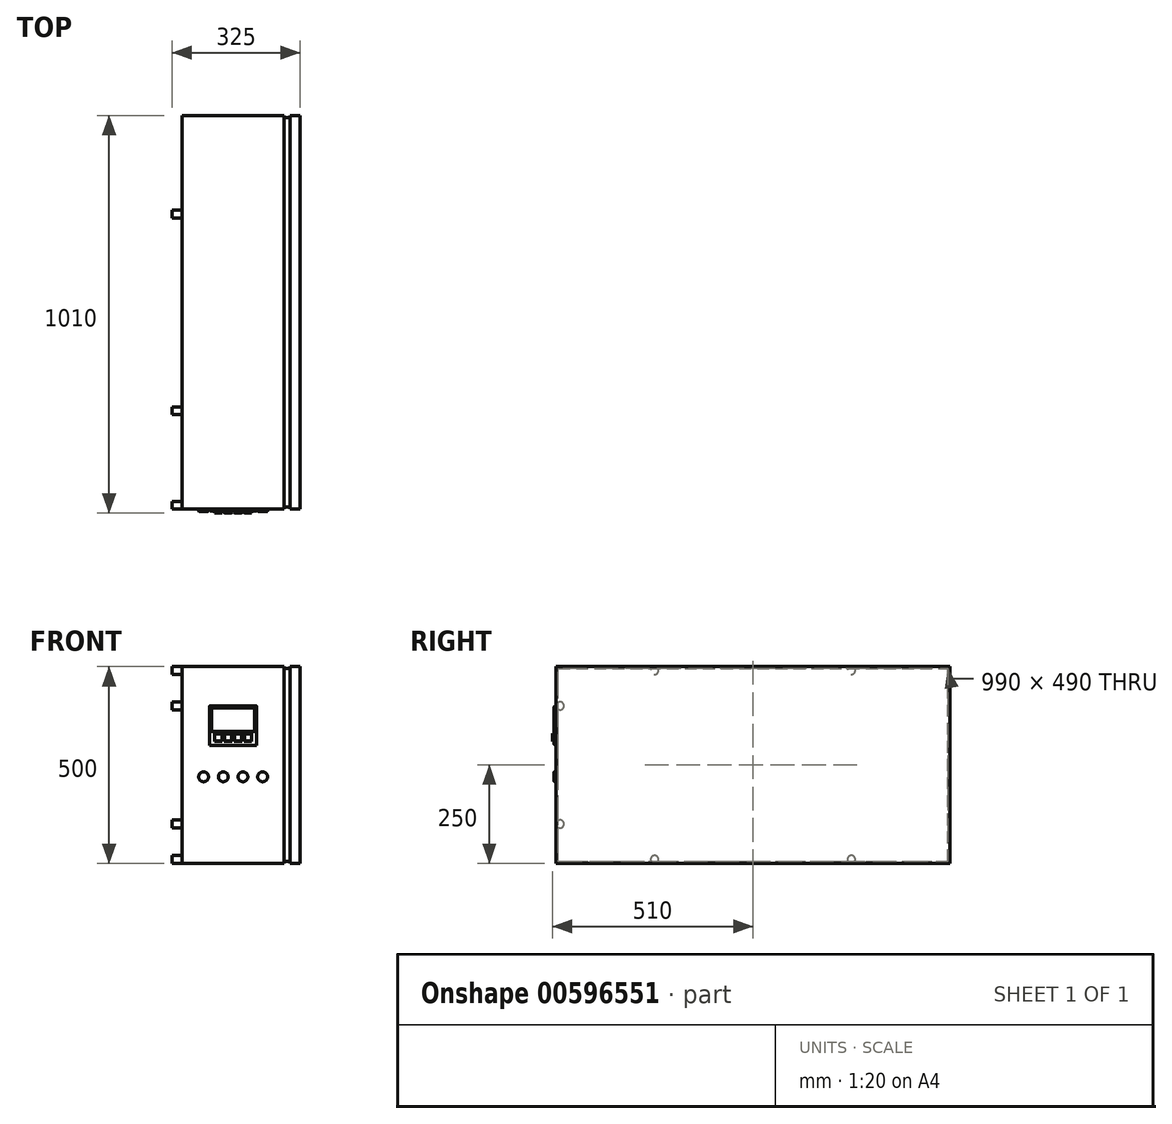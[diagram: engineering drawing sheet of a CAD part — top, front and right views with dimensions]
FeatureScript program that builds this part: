
annotation { "Feature Type Name" : "Feature", "Feature Type Description" : "" }
export const myFeature = defineFeature(function(context is Context, id is Id, definition is map)
    precondition{}
    {
        {
            var Q0;
            Q0=qCreatedBy(makeId("Front.planeOp"),FACE);
            var sketch = newSketch(context, id + "F0", { "sketchPlane" : qUnion([Q0])});
            skPoint(sketch, "E0.0", {"position": v(0, 0) * mm});
            skLineSegment(sketch, "E1.bottom", {"start": v(0, 0) * mm, "end": v(300, 0) * mm});
            skLineSegment(sketch, "E1.top", {"start": v(0, 500) * mm, "end": v(300, 500) * mm});
            skLineSegment(sketch, "E1.left", {"start": v(0, 0) * mm, "end": v(0, 500) * mm});
            skLineSegment(sketch, "E1.right", {"start": v(300, 0) * mm, "end": v(300, 500) * mm});
            skSolve(sketch);
        }
        {
            var Q0;
            Q0 = qSketchRegion(id + "F0", true);
            extrude(context, id + "F1", {"entities" : qUnion([Q0]), "depth" : 1000 * mm, "offsetDistance" : 25 * mm});
        }
        {
            var Q0;
            Q0=makeQuery(id+"F1.opExtrude","SWEPT_FACE",FACE,{"disambiguationData":[OSD([sQuery(id+"F0.wireOp",EDGE,"E1.right")])]});
            cPlane(context, id + "F2", {"entities" : qUnion([Q0]), "cplaneType" : CPlaneType.OFFSET, "offset" : 25 * mm, "oppositeDirection" : true, "width" : 150 * mm, "height" : 150 * mm});
        }
        {
            var Q0;
            Q0=qCreatedBy(id+"F2.planeOp",FACE);
            var sketch = newSketch(context, id + "F3", { "sketchPlane" : qUnion([Q0])});
            skLineSegment(sketch, "E2.bottom", {"start": v(-1000, 0) * mm, "end": v(0, 0) * mm});
            skLineSegment(sketch, "E2.top", {"start": v(-1000, 500) * mm, "end": v(0, 500) * mm});
            skLineSegment(sketch, "E2.left", {"start": v(-1000, 0) * mm, "end": v(-1000, 500) * mm});
            skLineSegment(sketch, "E2.right", {"start": v(0, 0) * mm, "end": v(0, 500) * mm});
            skLineSegment(sketch, "E3.bottom", {"start": v(-995, 5) * mm, "end": v(-5, 5) * mm});
            skLineSegment(sketch, "E3.top", {"start": v(-995, 495) * mm, "end": v(-5, 495) * mm});
            skLineSegment(sketch, "E3.left", {"start": v(-995, 5) * mm, "end": v(-995, 495) * mm});
            skLineSegment(sketch, "E3.right", {"start": v(-5, 5) * mm, "end": v(-5, 495) * mm});
            skSolve(sketch);
        }
        {
            var Q0;
            Q0 = qSketchRegion(id + "F3", true);
            extrude(context, id + "F4", {"entities" : qUnion([Q0]), "operationType" : NewBodyOperationType.REMOVE, "oppositeDirection" : true, "depth" : 15 * mm, "offsetDistance" : 25 * mm});
        }
        {
            var Q0;
            Q0=makeQuery(id+"F1.opExtrude","SWEPT_FACE",FACE,{"disambiguationData":[OSD([sQuery(id+"F0.wireOp",EDGE,"E1.left")])]});
            var sketch = newSketch(context, id + "F5", { "sketchPlane" : qUnion([Q0])});
            skCircle(sketch, "E4", {"center": v(250, 490) * mm, "radius": 10 * mm});
            skCircle(sketch, "E5", {"center": v(750, 490) * mm, "radius": 10 * mm});
            skCircle(sketch, "E6", {"center": v(250, 10) * mm, "radius": 10 * mm});
            skCircle(sketch, "E7", {"center": v(750, 10) * mm, "radius": 10 * mm});
            skCircle(sketch, "E8", {"center": v(990, 100) * mm, "radius": 10 * mm});
            skCircle(sketch, "E9", {"center": v(990, 400) * mm, "radius": 10 * mm});
            skSolve(sketch);
        }
        {
            var Q0;
            Q0 = qSketchRegion(id + "F5", true);
            extrude(context, id + "F6", {"entities" : qUnion([Q0]), "operationType" : NewBodyOperationType.ADD, "depth" : 25 * mm, "offsetDistance" : 25 * mm});
        }
        {
            var Q0;
            {var subQ0=sQuery(id+"F0.wireOp",EDGE,"E1.bottom");var subQ1=sQuery(id+"F0.wireOp",EDGE,"E1.top");var subQ2=sQuery(id+"F0.wireOp",EDGE,"E1.left");Q0=makeQuery(id+"F4.boolean.opBoolean","SPLIT",FACE,{"disambiguationData":[TD([makeQuery(id+"F1.opExtrude","SWEPT_FACE",FACE,{"disambiguationData":[OSD([subQ2])]})])],"derivedFrom":makeQuery(id+"F1.opExtrude","CAP_FACE",FACE,{"disambiguationData":[OSD([subQ0,subQ1,subQ2,sQuery(id+"F0.wireOp",EDGE,"E1.right")])],"isStart":false})});}
            var sketch = newSketch(context, id + "F7", { "sketchPlane" : qUnion([Q0])});
            skLineSegment(sketch, "E10.bottom", {"start": v(70, 400) * mm, "end": v(190, 400) * mm});
            skLineSegment(sketch, "E10.top", {"start": v(70, 300) * mm, "end": v(190, 300) * mm});
            skLineSegment(sketch, "E10.left", {"start": v(70, 400) * mm, "end": v(70, 300) * mm});
            skLineSegment(sketch, "E10.right", {"start": v(190, 400) * mm, "end": v(190, 300) * mm});
            skSolve(sketch);
        }
        {
            var Q0;
            Q0=makeQuery(id+"F7.imprint","IMPRINT",FACE,{"disambiguationData":[TD([[makeQuery(id+"F7.imprint","IMPRINT",EDGE,{"derivedFrom":sQuery(id+"F7.wireOp",EDGE,"E10.bottom")}),-1.0]])]});
            extrude(context, id + "F8", {"entities" : qUnion([Q0]), "depth" : 5 * mm, "offsetDistance" : 25 * mm});
        }
        {
            var Q0;
            Q0=makeQuery(id+"F8.opExtrude","CAP_FACE",FACE,{"disambiguationData":[OSD([sQuery(id+"F7.wireOp",EDGE,"E10.bottom"),sQuery(id+"F7.wireOp",EDGE,"E10.top"),sQuery(id+"F7.wireOp",EDGE,"E10.left"),sQuery(id+"F7.wireOp",EDGE,"E10.right")])],"isStart":false});
            var sketch = newSketch(context, id + "F9", { "sketchPlane" : qUnion([Q0])});
            skLineSegment(sketch, "E11.bottom", {"start": v(82.5, 330) * mm, "end": v(102.5, 330) * mm});
            skLineSegment(sketch, "E11.top", {"start": v(82.5, 310) * mm, "end": v(102.5, 310) * mm});
            skLineSegment(sketch, "E11.left", {"start": v(82.5, 330) * mm, "end": v(82.5, 310) * mm});
            skLineSegment(sketch, "E11.right", {"start": v(102.5, 330) * mm, "end": v(102.5, 310) * mm});
            skLineSegment(sketch, "E12.1.0.0", {"start": v(107.5, 330) * mm, "end": v(127.5, 330) * mm});
            skLineSegment(sketch, "E12.1.0.1", {"start": v(127.5, 330) * mm, "end": v(127.5, 310) * mm});
            skLineSegment(sketch, "E12.1.0.2", {"start": v(107.5, 310) * mm, "end": v(127.5, 310) * mm});
            skLineSegment(sketch, "E12.1.0.3", {"start": v(107.5, 330) * mm, "end": v(107.5, 310) * mm});
            skLineSegment(sketch, "E12.2.0.0", {"start": v(132.5, 330) * mm, "end": v(152.5, 330) * mm});
            skLineSegment(sketch, "E12.2.0.1", {"start": v(152.5, 330) * mm, "end": v(152.5, 310) * mm});
            skLineSegment(sketch, "E12.2.0.2", {"start": v(132.5, 310) * mm, "end": v(152.5, 310) * mm});
            skLineSegment(sketch, "E12.2.0.3", {"start": v(132.5, 330) * mm, "end": v(132.5, 310) * mm});
            skLineSegment(sketch, "E12.3.0.0", {"start": v(157.5, 330) * mm, "end": v(177.5, 330) * mm});
            skLineSegment(sketch, "E12.3.0.1", {"start": v(177.5, 330) * mm, "end": v(177.5, 310) * mm});
            skLineSegment(sketch, "E12.3.0.2", {"start": v(157.5, 310) * mm, "end": v(177.5, 310) * mm});
            skLineSegment(sketch, "E12.3.0.3", {"start": v(157.5, 330) * mm, "end": v(157.5, 310) * mm});
            skLineSegment(sketch, "E12.direction1", {"start": v(82.5, 330) * mm, "end": v(107.5, 330) * mm, "construction": true});
            skSolve(sketch);
        }
        {
            var Q0;
            Q0=makeQuery(id+"F9.imprint","IMPRINT",FACE,{"disambiguationData":[TD([[makeQuery(id+"F9.imprint","IMPRINT",EDGE,{"derivedFrom":sQuery(id+"F9.wireOp",EDGE,"E11.bottom")}),-1.0]])]});
            var Q1;
            Q1=makeQuery(id+"F9.imprint","IMPRINT",FACE,{"disambiguationData":[TD([[makeQuery(id+"F9.imprint","IMPRINT",EDGE,{"derivedFrom":sQuery(id+"F9.wireOp",EDGE,"E12.1.0.0")}),-1.0]])]});
            var Q2;
            Q2=makeQuery(id+"F9.imprint","IMPRINT",FACE,{"disambiguationData":[TD([[makeQuery(id+"F9.imprint","IMPRINT",EDGE,{"derivedFrom":sQuery(id+"F9.wireOp",EDGE,"E12.2.0.0")}),-1.0]])]});
            var Q3;
            Q3=makeQuery(id+"F9.imprint","IMPRINT",FACE,{"disambiguationData":[TD([[makeQuery(id+"F9.imprint","IMPRINT",EDGE,{"derivedFrom":sQuery(id+"F9.wireOp",EDGE,"E12.3.0.0")}),-1.0]])]});
            extrude(context, id + "F10", {"entities" : qUnion([Q0, Q1, Q2, Q3]), "operationType" : NewBodyOperationType.ADD, "depth" : 5 * mm, "offsetDistance" : 25 * mm});
        }
        {
            var Q0;
            Q0=makeQuery(id+"F8.opExtrude","CAP_FACE",FACE,{"disambiguationData":[OSD([sQuery(id+"F7.wireOp",EDGE,"E10.bottom"),sQuery(id+"F7.wireOp",EDGE,"E10.top"),sQuery(id+"F7.wireOp",EDGE,"E10.left"),sQuery(id+"F7.wireOp",EDGE,"E10.right")])],"isStart":false});
            var sketch = newSketch(context, id + "F11", { "sketchPlane" : qUnion([Q0])});
            skLineSegment(sketch, "E13.bottom", {"start": v(75, 395) * mm, "end": v(185, 395) * mm});
            skLineSegment(sketch, "E13.top", {"start": v(75, 335) * mm, "end": v(185, 335) * mm});
            skLineSegment(sketch, "E13.left", {"start": v(75, 395) * mm, "end": v(75, 335) * mm});
            skLineSegment(sketch, "E13.right", {"start": v(185, 395) * mm, "end": v(185, 335) * mm});
            skSolve(sketch);
        }
        {
            var Q0;
            Q0=makeQuery(id+"F11.imprint","IMPRINT",FACE,{"disambiguationData":[TD([[makeQuery(id+"F11.imprint","IMPRINT",EDGE,{"derivedFrom":sQuery(id+"F11.wireOp",EDGE,"E13.bottom")}),-1.0]])]});
            extrude(context, id + "F12", {"entities" : qUnion([Q0]), "operationType" : NewBodyOperationType.REMOVE, "oppositeDirection" : true, "depth" : 2 * mm, "offsetDistance" : 25 * mm});
        }
        {
            var Q0;
            {var subQ0=sQuery(id+"F0.wireOp",EDGE,"E1.bottom");var subQ1=sQuery(id+"F0.wireOp",EDGE,"E1.top");var subQ2=sQuery(id+"F0.wireOp",EDGE,"E1.left");Q0=makeQuery(id+"F4.boolean.opBoolean","SPLIT",FACE,{"disambiguationData":[TD([makeQuery(id+"F1.opExtrude","SWEPT_FACE",FACE,{"disambiguationData":[OSD([subQ2])]})])],"derivedFrom":makeQuery(id+"F1.opExtrude","CAP_FACE",FACE,{"disambiguationData":[OSD([subQ0,subQ1,subQ2,sQuery(id+"F0.wireOp",EDGE,"E1.right")])],"isStart":false})});}
            var sketch = newSketch(context, id + "F13", { "sketchPlane" : qUnion([Q0])});
            skSolve(sketch);
        }
        {
            var Q0;
            {var subQ0=sQuery(id+"F0.wireOp",EDGE,"E1.left");Q0=makeQuery(id+"F13.imprint","IMPRINT",FACE,{"disambiguationData":[TD([[makeQuery(id+"F13.imprint","IMPRINT",EDGE,{"derivedFrom":makeQuery(id+"F1.opExtrude","CAP_EDGE",EDGE,{"disambiguationData":[OSD([subQ0])],"isStart":false})}),-1.0]])]});}
            var sketch = newSketch(context, id + "F14", { "sketchPlane" : qUnion([Q0])});
            skCircle(sketch, "E14", {"center": v(55, 220) * mm, "radius": 12.5 * mm});
            skCircle(sketch, "E15.1.0.0", {"center": v(105, 220) * mm, "radius": 12.5 * mm});
            skCircle(sketch, "E15.2.0.0", {"center": v(155, 220) * mm, "radius": 12.5 * mm});
            skCircle(sketch, "E15.3.0.0", {"center": v(205, 220) * mm, "radius": 12.5 * mm});
            skLineSegment(sketch, "E15.direction1", {"start": v(55, 220) * mm, "end": v(105, 220) * mm, "construction": true});
            skSolve(sketch);
        }
        {
            var Q0;
            Q0 = qSketchRegion(id + "F14", true);
            extrude(context, id + "F15", {"entities" : qUnion([Q0]), "depth" : 6 * mm, "offsetDistance" : 25 * mm});
        }
        {
            var Q0;
            Q0=makeQuery(id+"F15.opExtrude","CAP_EDGE",EDGE,{"disambiguationData":[OSD([sQuery(id+"F14.wireOp",EDGE,"E14")])],"isStart":false});
            var Q1;
            Q1=makeQuery(id+"F15.opExtrude","CAP_EDGE",EDGE,{"disambiguationData":[OSD([sQuery(id+"F14.wireOp",EDGE,"E15.1.0.0")])],"isStart":false});
            var Q2;
            Q2=makeQuery(id+"F15.opExtrude","CAP_EDGE",EDGE,{"disambiguationData":[OSD([sQuery(id+"F14.wireOp",EDGE,"E15.2.0.0")])],"isStart":false});
            var Q3;
            Q3=makeQuery(id+"F15.opExtrude","CAP_EDGE",EDGE,{"disambiguationData":[OSD([sQuery(id+"F14.wireOp",EDGE,"E15.3.0.0")])],"isStart":false});
            fillet(context, id + "F16", {"entities" : qUnion([Q0, Q1, Q2, Q3]), "radius" : 2 * mm, "tangentPropagation" : true, "allowEdgeOverflow" : false});
        }
        {
            var Q0;
            Q0=makeQuery(id+"F8.opExtrude","CAP_EDGE",EDGE,{"disambiguationData":[OSD([sQuery(id+"F7.wireOp",EDGE,"E10.left")])],"isStart":false});
            var Q1;
            Q1=makeQuery(id+"F8.opExtrude","CAP_EDGE",EDGE,{"disambiguationData":[OSD([sQuery(id+"F7.wireOp",EDGE,"E10.top")])],"isStart":false});
            var Q2;
            Q2=makeQuery(id+"F8.opExtrude","CAP_EDGE",EDGE,{"disambiguationData":[OSD([sQuery(id+"F7.wireOp",EDGE,"E10.right")])],"isStart":false});
            var Q3;
            Q3=makeQuery(id+"F8.opExtrude","CAP_EDGE",EDGE,{"disambiguationData":[OSD([sQuery(id+"F7.wireOp",EDGE,"E10.bottom")])],"isStart":false});
            fillet(context, id + "F17", {"entities" : qUnion([Q0, Q1, Q2, Q3]), "radius" : 3 * mm, "tangentPropagation" : true, "allowEdgeOverflow" : false});
        }
        {
            var Q0;
            Q0=makeQuery(id+"F10.opExtrude","CAP_FACE",FACE,{"disambiguationData":[OSD([sQuery(id+"F9.wireOp",EDGE,"E11.bottom"),sQuery(id+"F9.wireOp",EDGE,"E11.top"),sQuery(id+"F9.wireOp",EDGE,"E11.left"),sQuery(id+"F9.wireOp",EDGE,"E11.right")])],"isStart":false});
            var Q1;
            Q1=makeQuery(id+"F10.opExtrude","CAP_FACE",FACE,{"disambiguationData":[OSD([sQuery(id+"F9.wireOp",EDGE,"E12.1.0.0"),sQuery(id+"F9.wireOp",EDGE,"E12.1.0.1"),sQuery(id+"F9.wireOp",EDGE,"E12.1.0.2"),sQuery(id+"F9.wireOp",EDGE,"E12.1.0.3")])],"isStart":false});
            var Q2;
            Q2=makeQuery(id+"F10.opExtrude","CAP_FACE",FACE,{"disambiguationData":[OSD([sQuery(id+"F9.wireOp",EDGE,"E12.2.0.0"),sQuery(id+"F9.wireOp",EDGE,"E12.2.0.1"),sQuery(id+"F9.wireOp",EDGE,"E12.2.0.2"),sQuery(id+"F9.wireOp",EDGE,"E12.2.0.3")])],"isStart":false});
            var Q3;
            Q3=makeQuery(id+"F10.opExtrude","CAP_FACE",FACE,{"disambiguationData":[OSD([sQuery(id+"F9.wireOp",EDGE,"E12.3.0.0"),sQuery(id+"F9.wireOp",EDGE,"E12.3.0.1"),sQuery(id+"F9.wireOp",EDGE,"E12.3.0.2"),sQuery(id+"F9.wireOp",EDGE,"E12.3.0.3")])],"isStart":false});
            chamfer(context, id + "F18", {"entities" : qUnion([Q0, Q1, Q2, Q3]), "width" : 1 * mm, "tangentPropagation" : true});
        }
        {
            var Q0;
            Q0=makeQuery(id+"F12.boolean.opBoolean","COPY",FACE,{"derivedFrom":makeQuery(id+"F12.opExtrude","CAP_FACE",FACE,{"disambiguationData":[OSD([sQuery(id+"F11.wireOp",EDGE,"E13.bottom"),sQuery(id+"F11.wireOp",EDGE,"E13.top"),sQuery(id+"F11.wireOp",EDGE,"E13.left"),sQuery(id+"F11.wireOp",EDGE,"E13.right")])],"isStart":false})});
            fillet(context, id + "F19", {"entities" : qUnion([Q0]), "radius" : 1 * mm, "tangentPropagation" : true, "allowEdgeOverflow" : false});
        }
    });
